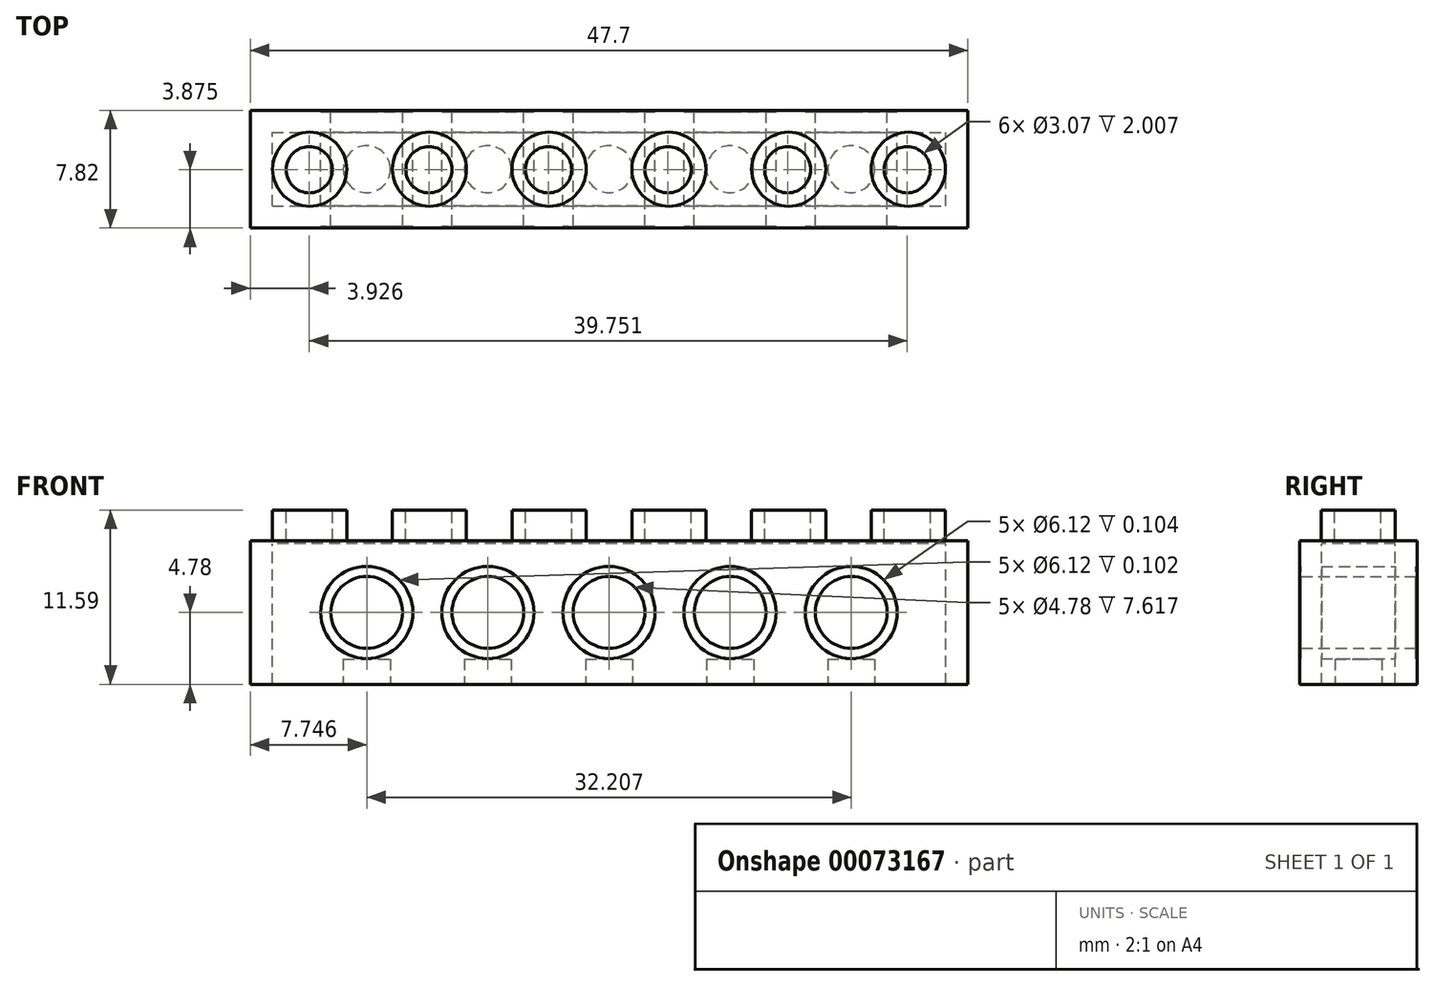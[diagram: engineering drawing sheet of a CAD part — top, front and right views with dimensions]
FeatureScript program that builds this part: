
annotation { "Feature Type Name" : "Feature", "Feature Type Description" : "" }
export const myFeature = defineFeature(function(context is Context, id is Id, definition is map)
    precondition{}
    {
        {
            var Q0;
            Q0=qCreatedBy(makeId("Front.planeOp"),FACE);
            var sketch = newSketch(context, id + "F0", { "sketchPlane" : qUnion([Q0])});
            skLineSegment(sketch, "E0.bottom", {"start": v(23.85, -4.78) * mm, "end": v(-23.85, -4.78) * mm});
            skLineSegment(sketch, "E0.top", {"start": v(23.85, 4.78) * mm, "end": v(-23.85, 4.78) * mm});
            skLineSegment(sketch, "E0.left", {"start": v(23.85, -4.78) * mm, "end": v(23.85, 4.78) * mm});
            skLineSegment(sketch, "E0.right", {"start": v(-23.85, -4.78) * mm, "end": v(-23.85, 4.78) * mm});
            skPoint(sketch, "E0.middle", {"position": v(0, 0) * mm});
            skSolve(sketch);
        }
        {
            var Q0;
            Q0=qSketchRegion(id+"F0",true);
            extrude(context, id + "F1", {"entities" : qUnion([Q0]), "depth" : 7.82 * mm});
        }
        {
            var Q0;
            Q0=qCreatedBy(makeId("Top.planeOp"),FACE);
            var sketch = newSketch(context, id + "F2", { "sketchPlane" : qUnion([Q0])});
            skLineSegment(sketch, "E1", {"start": v(0, -7.82) * mm, "end": v(0, 0) * mm});
            skLineSegment(sketch, "E2.bottom", {"start": v(22.4, -1.46) * mm, "end": v(-22.4, -1.46) * mm});
            skLineSegment(sketch, "E2.top", {"start": v(22.4, -6.36) * mm, "end": v(-22.4, -6.36) * mm});
            skLineSegment(sketch, "E2.left", {"start": v(22.4, -1.46) * mm, "end": v(22.4, -6.36) * mm});
            skLineSegment(sketch, "E2.right", {"start": v(-22.4, -1.46) * mm, "end": v(-22.4, -6.36) * mm});
            skPoint(sketch, "E2.middle", {"position": v(0, -3.91) * mm});
            skSolve(sketch);
        }
        {
            var Q0;
            Q0=qSketchRegion(id+"F2",true);
            extrude(context, id + "F3", {"entities" : qUnion([Q0]), "operationType" : NewBodyOperationType.REMOVE, "endBound" : BoundingType.THROUGH_ALL, "oppositeDirection" : true, "depth" : 5.34 * mm, "hasSecondDirection" : true, "secondDirectionOppositeDirection" : false, "secondDirectionDepth" : 4.57 * mm});
        }
        {
            var Q0;
            Q0=qCreatedBy(makeId("Top.planeOp"),FACE);
            var sketch = newSketch(context, id + "F4", { "sketchPlane" : qUnion([Q0])});
            skLineSegment(sketch, "E3", {"start": v(-19.9, 0) * mm, "end": v(-19.9, -7.82) * mm, "construction": true});
            skCircle(sketch, "E4", {"center": v(-19.9, -3.91) * mm, "radius": 2.46 * mm});
            skLineSegment(sketch, "E5", {"start": v(-23.85, 0) * mm, "end": v(-23.85, -7.82) * mm});
            skLineSegment(sketch, "E6", {"start": v(-23.85, 0) * mm, "end": v(0, 0) * mm});
            skCircle(sketch, "E7.1.0.0", {"center": v(-11.94, -3.91) * mm, "radius": 2.46 * mm});
            skCircle(sketch, "E7.2.0.0", {"center": v(-3.98, -3.91) * mm, "radius": 2.46 * mm});
            skCircle(sketch, "E7.3.0.0", {"center": v(3.98, -3.91) * mm, "radius": 2.46 * mm});
            skCircle(sketch, "E7.4.0.0", {"center": v(11.94, -3.91) * mm, "radius": 2.46 * mm});
            skCircle(sketch, "E7.5.0.0", {"center": v(19.9, -3.91) * mm, "radius": 2.46 * mm});
            skLineSegment(sketch, "E7.direction1", {"start": v(-19.9, -3.91) * mm, "end": v(-11.94, -3.91) * mm, "construction": true});
            skSolve(sketch);
        }
        {
            var Q0;
            Q0=makeQuery(id+"F4.imprint","IMPRINT",FACE,{"disambiguationData":[TD([[makeQuery(id+"F4.imprint","IMPRINT",EDGE,{"derivedFrom":sQuery(id+"F4.wireOp",EDGE,"E4")}),1.0]])]});
            var Q1;
            Q1=makeQuery(id+"F4.imprint","IMPRINT",FACE,{"disambiguationData":[TD([[makeQuery(id+"F4.imprint","IMPRINT",EDGE,{"derivedFrom":sQuery(id+"F4.wireOp",EDGE,"E7.1.0.0")}),1.0]])]});
            var Q2;
            Q2=makeQuery(id+"F4.imprint","IMPRINT",FACE,{"disambiguationData":[TD([[makeQuery(id+"F4.imprint","IMPRINT",EDGE,{"derivedFrom":sQuery(id+"F4.wireOp",EDGE,"E7.2.0.0")}),1.0]])]});
            var Q3;
            Q3=makeQuery(id+"F4.imprint","IMPRINT",FACE,{"disambiguationData":[TD([[makeQuery(id+"F4.imprint","IMPRINT",EDGE,{"derivedFrom":sQuery(id+"F4.wireOp",EDGE,"E7.3.0.0")}),1.0]])]});
            var Q4;
            Q4=makeQuery(id+"F4.imprint","IMPRINT",FACE,{"disambiguationData":[TD([[makeQuery(id+"F4.imprint","IMPRINT",EDGE,{"derivedFrom":sQuery(id+"F4.wireOp",EDGE,"E7.4.0.0")}),1.0]])]});
            var Q5;
            Q5=makeQuery(id+"F4.imprint","IMPRINT",FACE,{"disambiguationData":[TD([[makeQuery(id+"F4.imprint","IMPRINT",EDGE,{"derivedFrom":sQuery(id+"F4.wireOp",EDGE,"E7.5.0.0")}),1.0]])]});
            extrude(context, id + "F5", {"entities" : qUnion([Q0, Q1, Q2, Q3, Q4, Q5]), "operationType" : NewBodyOperationType.ADD, "depth" : 6.8 * mm, "hasSecondDirection" : true, "secondDirectionOppositeDirection" : false, "secondDirectionDepth" : 4.66 * mm});
        }
        {
            var Q0;
            Q0=makeQuery(id+"F5.opExtrude","CAP_FACE",FACE,{"disambiguationData":[OSD([sQuery(id+"F4.wireOp",EDGE,"E4")])],"isStart":false});
            cPlane(context, id + "F6", {"entities" : qUnion([Q0]), "cplaneType" : CPlaneType.OFFSET, "offset" : 152.4 * mm, "width" : 152.4 * mm, "height" : 152.4 * mm});
        }
        {
            var Q0;
            Q0=qCreatedBy(id+"F6.planeOp",FACE);
            var sketch = newSketch(context, id + "F7", { "sketchPlane" : qUnion([Q0])});
            skCircle(sketch, "E8", {"center": v(19.83, -3.94) * mm, "radius": 1.54 * mm});
            skCircle(sketch, "E9.1.0.0", {"center": v(11.88, -3.94) * mm, "radius": 1.54 * mm});
            skCircle(sketch, "E9.2.0.0", {"center": v(3.93, -3.94) * mm, "radius": 1.54 * mm});
            skCircle(sketch, "E9.3.0.0", {"center": v(-4.02, -3.94) * mm, "radius": 1.54 * mm});
            skCircle(sketch, "E9.4.0.0", {"center": v(-11.97, -3.94) * mm, "radius": 1.54 * mm});
            skCircle(sketch, "E9.5.0.0", {"center": v(-19.92, -3.94) * mm, "radius": 1.54 * mm});
            skLineSegment(sketch, "E9.direction1", {"start": v(19.83, -3.94) * mm, "end": v(11.88, -3.94) * mm, "construction": true});
            skSolve(sketch);
        }
        {
            var Q0;
            Q0=qSketchRegion(id+"F7",true);
            extrude(context, id + "F8", {"entities" : qUnion([Q0]), "operationType" : NewBodyOperationType.REMOVE, "oppositeDirection" : true, "depth" : 154.4 * mm});
        }
        {
            var Q0;
            Q0=qCreatedBy(makeId("Front.planeOp"),FACE);
            var sketch = newSketch(context, id + "F9", { "sketchPlane" : qUnion([Q0])});
            skCircle(sketch, "E10", {"center": v(0, 0) * mm, "radius": 3.06 * mm});
            skCircle(sketch, "E11.1.0.0", {"center": v(8.05, 0) * mm, "radius": 3.06 * mm});
            skCircle(sketch, "E11.2.0.0", {"center": v(16.1, 0) * mm, "radius": 3.06 * mm});
            skLineSegment(sketch, "E11.direction1", {"start": v(0, 0) * mm, "end": v(8.05, 0) * mm, "construction": true});
            skCircle(sketch, "E12.2.0.0", {"center": v(-8.05, 0) * mm, "radius": 3.06 * mm});
            skCircle(sketch, "E12.3.0.0", {"center": v(-16.1, 0) * mm, "radius": 3.06 * mm});
            skLineSegment(sketch, "E12.direction1", {"start": v(8.05, 0) * mm, "end": v(0, 0) * mm, "construction": true});
            skSolve(sketch);
        }
        {
            var Q0;
            Q0=qSketchRegion(id+"F9",true);
            extrude(context, id + "F10", {"entities" : qUnion([Q0]), "operationType" : NewBodyOperationType.REMOVE, "depth" : 9.14 * mm});
        }
        {
            var Q0;
            Q0=qCreatedBy(makeId("Front.planeOp"),FACE);
            var sketch = newSketch(context, id + "F11", { "sketchPlane" : qUnion([Q0])});
            skCircle(sketch, "E13", {"center": v(0, 0) * mm, "radius": 2.39 * mm});
            skCircle(sketch, "E14", {"center": v(0, 0) * mm, "radius": 3.06 * mm});
            skCircle(sketch, "E15.1.0.0", {"center": v(8.05, 0) * mm, "radius": 2.39 * mm});
            skCircle(sketch, "E15.1.0.1", {"center": v(8.05, 0) * mm, "radius": 3.06 * mm});
            skCircle(sketch, "E15.2.0.0", {"center": v(16.1, 0) * mm, "radius": 2.39 * mm});
            skCircle(sketch, "E15.2.0.1", {"center": v(16.1, 0) * mm, "radius": 3.06 * mm});
            skLineSegment(sketch, "E15.direction1", {"start": v(0, 0) * mm, "end": v(8.05, 0) * mm, "construction": true});
            skCircle(sketch, "E16.2.0.0", {"center": v(-8.05, 0) * mm, "radius": 2.39 * mm});
            skCircle(sketch, "E16.2.0.1", {"center": v(-8.05, 0) * mm, "radius": 3.06 * mm});
            skCircle(sketch, "E16.3.0.0", {"center": v(-16.1, 0) * mm, "radius": 2.39 * mm});
            skCircle(sketch, "E16.3.0.1", {"center": v(-16.1, 0) * mm, "radius": 3.06 * mm});
            skLineSegment(sketch, "E16.direction1", {"start": v(8.05, 0) * mm, "end": v(0, 0) * mm, "construction": true});
            skSolve(sketch);
        }
        {
            var Q0;
            Q0=qSketchRegion(id+"F11",true);
            extrude(context, id + "F12", {"entities" : qUnion([Q0]), "operationType" : NewBodyOperationType.ADD, "depth" : 7.72 * mm, "hasSecondDirection" : true, "secondDirectionOppositeDirection" : false, "secondDirectionDepth" : 0.1 * mm});
        }
        {
            var Q0;
            Q0=makeQuery(id+"F1.opExtrude","SWEPT_FACE",FACE,{"disambiguationData":[OSD([sQuery(id+"F0.wireOp",EDGE,"E0.bottom")])]});
            cPlane(context, id + "F13", {"entities" : qUnion([Q0]), "cplaneType" : CPlaneType.OFFSET, "offset" : 0 * mm, "width" : 152.4 * mm, "height" : 152.4 * mm});
        }
        {
            var Q0;
            Q0=qCreatedBy(id+"F13.planeOp",FACE);
            var sketch = newSketch(context, id + "F14", { "sketchPlane" : qUnion([Q0])});
            skCircle(sketch, "E17", {"center": v(0, 3.91) * mm, "radius": 1.56 * mm});
            skLineSegment(sketch, "E18", {"start": v(0, 3.91) * mm, "end": v(0, 0) * mm, "construction": true});
            skCircle(sketch, "E19.1.0.0", {"center": v(8.05, 3.91) * mm, "radius": 1.56 * mm});
            skCircle(sketch, "E19.2.0.0", {"center": v(16.1, 3.91) * mm, "radius": 1.56 * mm});
            skLineSegment(sketch, "E19.direction1", {"start": v(0, 3.91) * mm, "end": v(8.05, 3.91) * mm, "construction": true});
            skCircle(sketch, "E20.2.0.0", {"center": v(-8.05, 3.91) * mm, "radius": 1.56 * mm});
            skCircle(sketch, "E20.3.0.0", {"center": v(-16.1, 3.91) * mm, "radius": 1.56 * mm});
            skLineSegment(sketch, "E20.direction1", {"start": v(8.05, 3.91) * mm, "end": v(0, 3.91) * mm, "construction": true});
            skSolve(sketch);
        }
        {
            var Q0;
            Q0=qSketchRegion(id+"F14",true);
            extrude(context, id + "F15", {"entities" : qUnion([Q0]), "oppositeDirection" : true, "depth" : 1.68 * mm});
        }
    });
